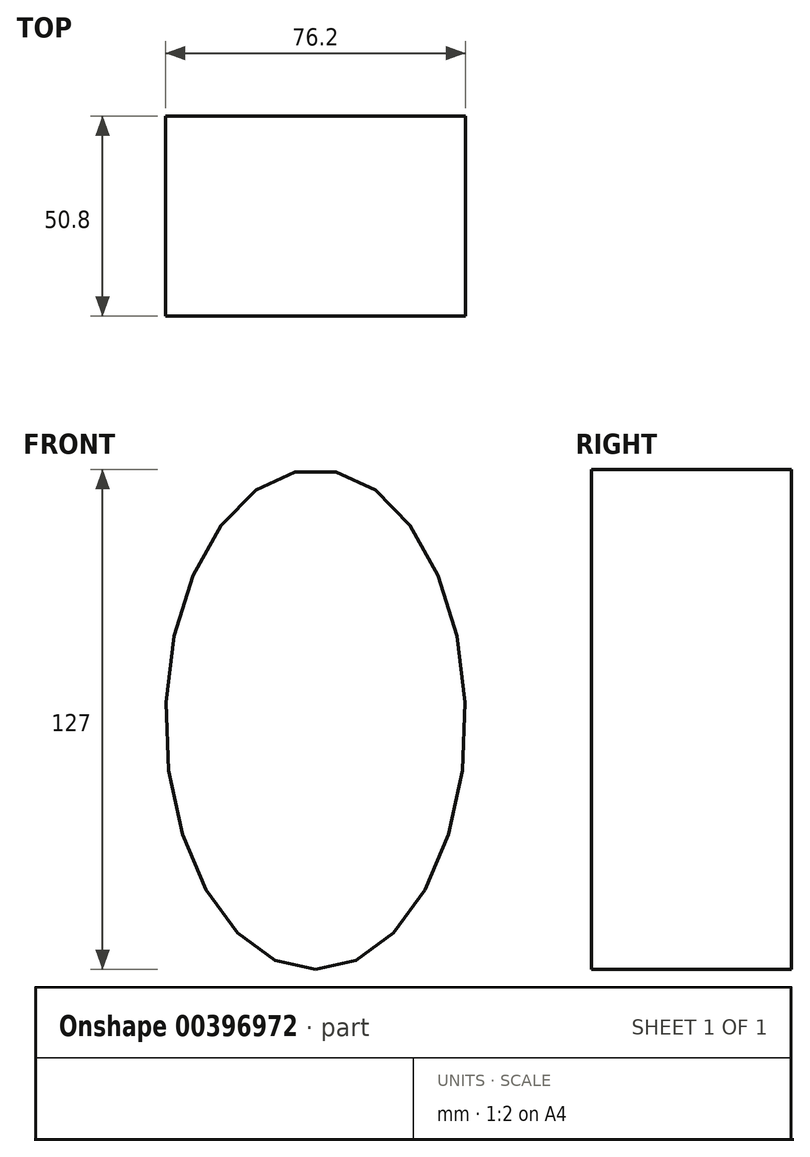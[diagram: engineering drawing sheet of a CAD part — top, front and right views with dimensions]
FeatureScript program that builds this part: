
annotation { "Feature Type Name" : "Feature", "Feature Type Description" : "" }
export const myFeature = defineFeature(function(context is Context, id is Id, definition is map)
    precondition{}
    {
        {
            var Q0;
            Q0=qCreatedBy(makeId("Front.planeOp"),FACE);
            var sketch = newSketch(context, id + "F0", { "sketchPlane" : qUnion([Q0])});
            skEllipse(sketch, "E0", {"center": v(0, 0) * mm, "majorRadius": 63.5 * mm, "minorRadius": 38.1 * mm, "majorAxis": v(0, -1)});
            skSolve(sketch);
        }
        {
            var Q0;
            Q0=makeQuery(id+"F0.imprint","IMPRINT",FACE,{"disambiguationData":[TD([[makeQuery(id+"F0.imprint","IMPRINT",EDGE,{"derivedFrom":sQuery(id+"F0.wireOp",EDGE,"E0")}),1.0]])]});
            extrude(context, id + "F1", {"entities" : qUnion([Q0]), "depth" : 50.8 * mm});
        }
    });
